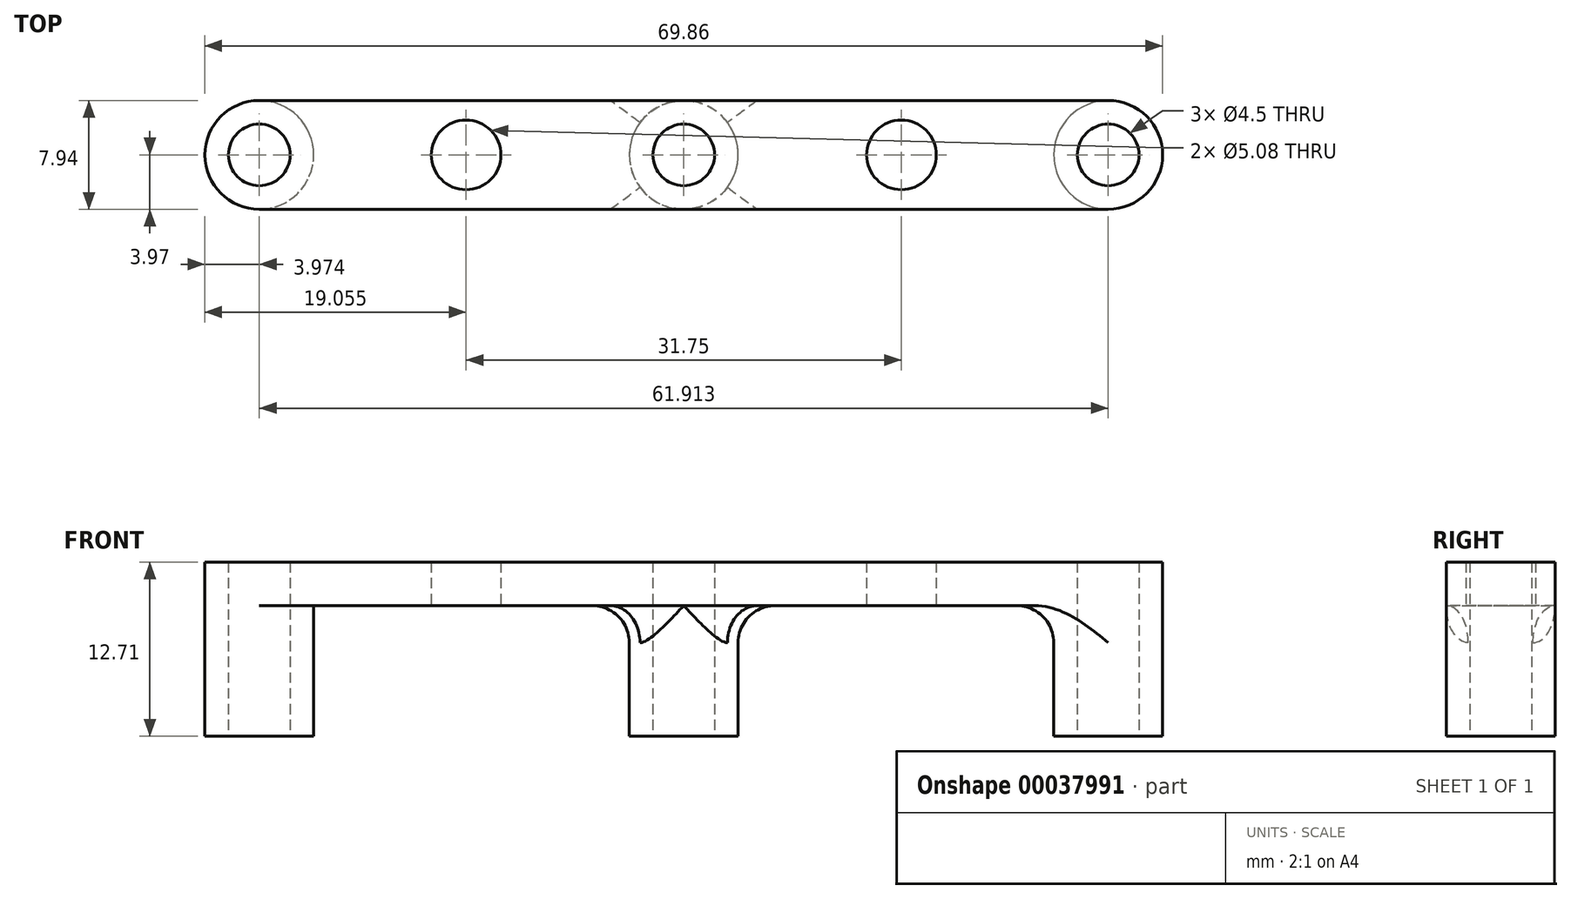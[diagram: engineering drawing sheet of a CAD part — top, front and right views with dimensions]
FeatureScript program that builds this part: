
annotation { "Feature Type Name" : "Feature", "Feature Type Description" : "" }
export const myFeature = defineFeature(function(context is Context, id is Id, definition is map)
    precondition{}
    {
        {
            var Q0;
            Q0=qCreatedBy(makeId("Top.planeOp"),FACE);
            var sketch = newSketch(context, id + "F0", { "sketchPlane" : qUnion([Q0])});
            skLineSegment(sketch, "E0.rect.bottom", {"start": v(30.96, 3.97) * mm, "end": v(-30.96, 3.97) * mm});
            skLineSegment(sketch, "E0.rect.top", {"start": v(30.96, -3.97) * mm, "end": v(-30.96, -3.97) * mm});
            skLineSegment(sketch, "E0.rect.left", {"start": v(30.96, 3.97) * mm, "end": v(30.96, -3.97) * mm});
            skLineSegment(sketch, "E0.rect.right", {"start": v(-30.96, 3.97) * mm, "end": v(-30.96, -3.97) * mm});
            skPoint(sketch, "E0.rect.middle", {"position": v(0, 0) * mm});
            skCircle(sketch, "E1", {"center": v(0, 0) * mm, "radius": 2.25 * mm});
            skCircle(sketch, "E2", {"center": v(30.96, 0) * mm, "radius": 2.25 * mm});
            skCircle(sketch, "E3", {"center": v(-30.96, 0) * mm, "radius": 2.25 * mm});
            skLineSegment(sketch, "E4", {"start": v(-15.88, 0) * mm, "end": v(15.88, 0) * mm, "construction": true});
            skCircle(sketch, "E5", {"center": v(-15.88, 0) * mm, "radius": 2.54 * mm});
            skCircle(sketch, "E6", {"center": v(15.88, 0) * mm, "radius": 2.54 * mm});
            skArc(sketch, "E7", {"start": v(-30.96, 3.97) * mm, "mid": v(-34.93, 0) * mm, "end": v(-30.96, -3.97) * mm});
            skArc(sketch, "E8", {"start": v(30.96, -3.97) * mm, "mid": v(34.93, 0) * mm, "end": v(30.96, 3.97) * mm});
            skLineSegment(sketch, "E9", {"start": v(15.88, 0) * mm, "end": v(30.96, 0) * mm, "construction": true});
            skSolve(sketch);
        }
        {
            var Q0;
            Q0=qSketchRegion(id+"F0",true);
            extrude(context, id + "F1", {"entities" : qUnion([Q0]), "depth" : 3.17 * mm});
        }
        {
            var Q0;
            Q0=makeQuery(id+"F1.opExtrude","CAP_FACE",FACE,{"disambiguationData":[OSD([sQuery(id+"F0.wireOp",EDGE,"E0.rect.bottom"),sQuery(id+"F0.wireOp",EDGE,"E0.rect.top"),sQuery(id+"F0.wireOp",EDGE,"E1"),sQuery(id+"F0.wireOp",EDGE,"E2"),sQuery(id+"F0.wireOp",EDGE,"E3"),sQuery(id+"F0.wireOp",EDGE,"E5"),sQuery(id+"F0.wireOp",EDGE,"E6"),sQuery(id+"F0.wireOp",EDGE,"E7"),sQuery(id+"F0.wireOp",EDGE,"E8")])],"isStart":true});
            var sketch = newSketch(context, id + "F2", { "sketchPlane" : qUnion([Q0])});
            skCircle(sketch, "E10", {"center": v(-30.96, 0) * mm, "radius": 3.97 * mm});
            skCircle(sketch, "E11", {"center": v(-30.96, 0) * mm, "radius": 2.25 * mm});
            skCircle(sketch, "E12", {"center": v(0, 0) * mm, "radius": 3.97 * mm});
            skCircle(sketch, "E13", {"center": v(0, 0) * mm, "radius": 2.25 * mm});
            skCircle(sketch, "E14", {"center": v(30.96, 0) * mm, "radius": 2.25 * mm});
            skCircle(sketch, "E15", {"center": v(30.96, 0) * mm, "radius": 3.97 * mm});
            skSolve(sketch);
        }
        {
            var Q0;
            Q0=qSketchRegion(id+"F2",true);
            extrude(context, id + "F3", {"entities" : qUnion([Q0]), "operationType" : NewBodyOperationType.ADD, "depth" : 9.52 * mm});
        }
        {
            var Q0;
            Q0=makeQuery(id+"F3.opExtrude","CAP_EDGE",EDGE,{"disambiguationData":[OSD([sQuery(id+"F2.wireOp",EDGE,"E10")])],"isStart":true});
            var Q1;
            Q1=makeQuery(id+"F3.boolean.opBoolean","SPLIT",EDGE,{"disambiguationData":[OD(1.0)],"derivedFrom":makeQuery(id+"F3.opExtrude","CAP_EDGE",EDGE,{"disambiguationData":[OSD([sQuery(id+"F2.wireOp",EDGE,"E12")])],"isStart":true})});
            var Q2;
            Q2=makeQuery(id+"F3.opExtrude","CAP_EDGE",EDGE,{"disambiguationData":[OSD([sQuery(id+"F2.wireOp",EDGE,"E15")])],"isStart":true});
            fillet(context, id + "F4", {"entities" : qUnion([Q0, Q1, Q2]), "radius" : 2.7 * mm, "tangentPropagation" : true, "allowEdgeOverflow" : false});
        }
    });
